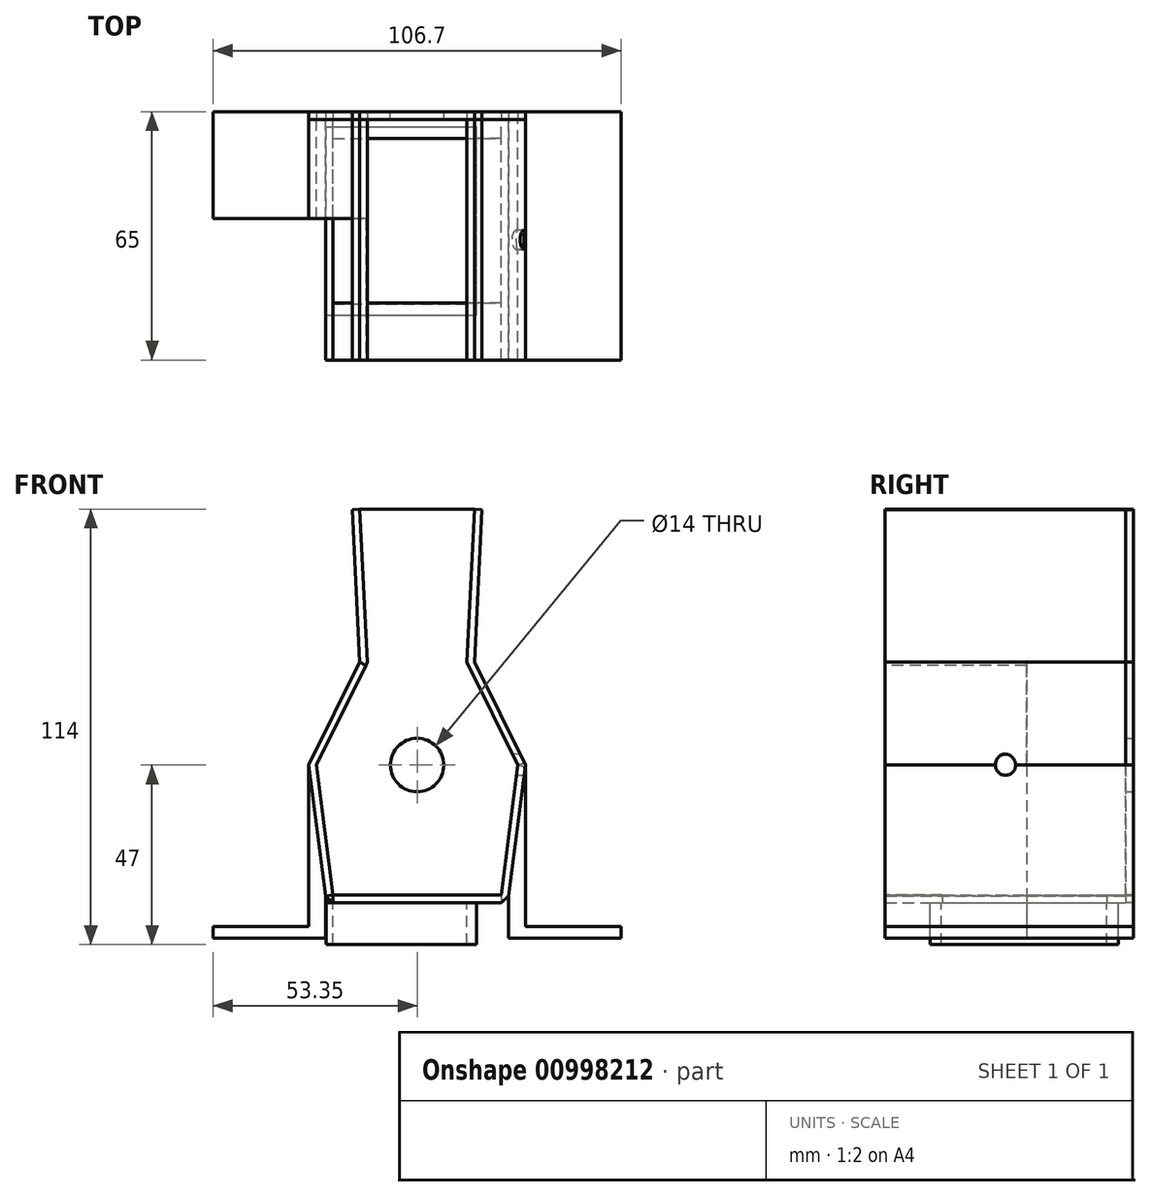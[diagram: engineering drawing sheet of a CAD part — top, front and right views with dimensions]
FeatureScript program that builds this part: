
annotation { "Feature Type Name" : "Feature", "Feature Type Description" : "" }
export const myFeature = defineFeature(function(context is Context, id is Id, definition is map)
    precondition{}
    {
        {
            var Q0;
            Q0=qCreatedBy(makeId("Front.planeOp"),FACE);
            var sketch = newSketch(context, id + "F0", { "sketchPlane" : qUnion([Q0])});
            skLineSegment(sketch, "E0.bottom", {"start": v(0, 0) * mm, "end": v(-26, 0) * mm});
            skLineSegment(sketch, "E0.top", {"start": v(0, 27) * mm, "end": v(-26, 27) * mm});
            skLineSegment(sketch, "E0.left", {"start": v(0, 0) * mm, "end": v(0, 27) * mm});
            skLineSegment(sketch, "E0.right", {"start": v(-26, 0) * mm, "end": v(-26, 27) * mm});
            skLineSegment(sketch, "E1", {"start": v(-26, 0) * mm, "end": v(-39.35, 0) * mm});
            skLineSegment(sketch, "E2", {"start": v(0, 0) * mm, "end": v(13.35, 0) * mm});
            skLineSegment(sketch, "E3", {"start": v(-26, 27) * mm, "end": v(-39.35, 0) * mm});
            skLineSegment(sketch, "E4", {"start": v(0, 27) * mm, "end": v(13.35, 0) * mm});
            skLineSegment(sketch, "E5.bottom", {"start": v(0, 0) * mm, "end": v(-13, 0) * mm});
            skLineSegment(sketch, "E5.top", {"start": v(0, -34) * mm, "end": v(-13, -34) * mm});
            skLineSegment(sketch, "E5.left", {"start": v(0, 0) * mm, "end": v(0, -34) * mm});
            skLineSegment(sketch, "E5.right", {"start": v(-13, 0) * mm, "end": v(-13, -34) * mm});
            skLineSegment(sketch, "E6.bottom", {"start": v(-26, 0) * mm, "end": v(-13, 0) * mm});
            skLineSegment(sketch, "E6.top", {"start": v(-26, -34) * mm, "end": v(-13, -34) * mm});
            skLineSegment(sketch, "E6.left", {"start": v(-26, 0) * mm, "end": v(-26, -34) * mm});
            skLineSegment(sketch, "E7", {"start": v(-26, -34) * mm, "end": v(-35, -34) * mm});
            skLineSegment(sketch, "E8", {"start": v(0, -34) * mm, "end": v(9, -34) * mm});
            skLineSegment(sketch, "E9", {"start": v(-35, -34) * mm, "end": v(-39.35, 0) * mm});
            skLineSegment(sketch, "E10", {"start": v(13.35, 0) * mm, "end": v(9, -34) * mm});
            skCircle(sketch, "E11", {"center": v(-13, 0) * mm, "radius": 7 * mm});
            skLineSegment(sketch, "E12.bottom", {"start": v(-26, 27) * mm, "end": v(0, 27) * mm});
            skLineSegment(sketch, "E12.top", {"start": v(-26, 67) * mm, "end": v(0, 67) * mm});
            skLineSegment(sketch, "E12.left", {"start": v(-26, 27) * mm, "end": v(-26, 67) * mm});
            skLineSegment(sketch, "E12.right", {"start": v(0, 27) * mm, "end": v(0, 67) * mm});
            skLineSegment(sketch, "E13", {"start": v(-26, 67) * mm, "end": v(-28, 67) * mm});
            skLineSegment(sketch, "E14", {"start": v(0, 67) * mm, "end": v(2, 67) * mm});
            skLineSegment(sketch, "E15", {"start": v(-26, 27) * mm, "end": v(-28, 67) * mm});
            skLineSegment(sketch, "E16", {"start": v(2, 67) * mm, "end": v(0, 27) * mm});
            skSolve(sketch);
        }
        {
            var Q0;
            Q0=makeQuery(id+"F0.imprint","IMPRINT",FACE,{"disambiguationData":[TD([[makeQuery(id+"F0.imprint","IMPRINT",EDGE,{"derivedFrom":sQuery(id+"F0.wireOp",EDGE,"E0.top")}),-1.0]])]});
            var Q1;
            Q1=makeQuery(id+"F0.imprint","IMPRINT",FACE,{"disambiguationData":[TD([[makeQuery(id+"F0.imprint","IMPRINT",EDGE,{"derivedFrom":sQuery(id+"F0.wireOp",EDGE,"E12.left")}),1.0]])]});
            var Q2;
            Q2=makeQuery(id+"F0.imprint","IMPRINT",FACE,{"disambiguationData":[TD([[makeQuery(id+"F0.imprint","IMPRINT",EDGE,{"derivedFrom":sQuery(id+"F0.wireOp",EDGE,"E12.right")}),-1.0]])]});
            var Q3;
            Q3=makeQuery(id+"F0.imprint","IMPRINT",FACE,{"disambiguationData":[TD([[makeQuery(id+"F0.imprint","IMPRINT",EDGE,{"derivedFrom":sQuery(id+"F0.wireOp",EDGE,"E0.top")}),1.0]])]});
            var Q4;
            Q4=makeQuery(id+"F0.imprint","IMPRINT",FACE,{"disambiguationData":[TD([[makeQuery(id+"F0.imprint","IMPRINT",EDGE,{"derivedFrom":sQuery(id+"F0.wireOp",EDGE,"E0.right")}),1.0]])]});
            var Q5;
            Q5=makeQuery(id+"F0.imprint","IMPRINT",FACE,{"disambiguationData":[TD([[makeQuery(id+"F0.imprint","IMPRINT",EDGE,{"derivedFrom":sQuery(id+"F0.wireOp",EDGE,"E0.left")}),-1.0]])]});
            var Q6;
            Q6=makeQuery(id+"F0.imprint","IMPRINT",FACE,{"disambiguationData":[TD([[makeQuery(id+"F0.imprint","IMPRINT",EDGE,{"derivedFrom":sQuery(id+"F0.wireOp",EDGE,"E2")}),-1.0]])]});
            var Q7;
            {var subQ1=sQuery(id+"F0.wireOp",EDGE,"E6.top");Q7=makeQuery(id+"F0.imprint","IMPRINT",FACE,{"disambiguationData":[TD([[makeQuery(id+"F0.imprint","IMPRINT",EDGE,{"derivedFrom":subQ1}),1.0]])]});}
            var Q8;
            Q8=makeQuery(id+"F0.imprint","IMPRINT",FACE,{"disambiguationData":[TD([[makeQuery(id+"F0.imprint","IMPRINT",EDGE,{"derivedFrom":sQuery(id+"F0.wireOp",EDGE,"E1")}),1.0]])]});
            var Q9;
            {var subQ1=sQuery(id+"F0.wireOp",EDGE,"E5.top");Q9=makeQuery(id+"F0.imprint","IMPRINT",FACE,{"disambiguationData":[TD([[makeQuery(id+"F0.imprint","IMPRINT",EDGE,{"derivedFrom":subQ1}),-1.0]])]});}
            var Q10;
            Q10 = qSketchRegion(id + "F2", true);
            extrude(context, id + "F1", {"entities" : qUnion([Q0, Q1, Q2, Q3, Q4, Q5, Q6, Q7, Q8, Q9, Q10]), "depth" : 2 * mm, "offsetDistance" : 25 * mm});
        }
        {
            var Q0;
            Q0=makeQuery(id+"F1.opExtrude","CAP_FACE",FACE,{"disambiguationData":[OSD([sQuery(id+"F0.wireOp",EDGE,"E3"),sQuery(id+"F0.wireOp",EDGE,"E4"),sQuery(id+"F0.wireOp",EDGE,"E5.top"),sQuery(id+"F0.wireOp",EDGE,"E6.top"),sQuery(id+"F0.wireOp",EDGE,"E7"),sQuery(id+"F0.wireOp",EDGE,"E8"),sQuery(id+"F0.wireOp",EDGE,"E9"),sQuery(id+"F0.wireOp",EDGE,"E10"),sQuery(id+"F0.wireOp",EDGE,"E11"),sQuery(id+"F0.wireOp",EDGE,"E12.top"),sQuery(id+"F0.wireOp",EDGE,"E13"),sQuery(id+"F0.wireOp",EDGE,"E14"),sQuery(id+"F0.wireOp",EDGE,"E15"),sQuery(id+"F0.wireOp",EDGE,"E16")])],"isStart":false});
            var sketch = newSketch(context, id + "F2", { "sketchPlane" : qUnion([Q0])});
            skLineSegment(sketch, "E17", {"start": v(-28, 67) * mm, "end": v(-30, 66.9) * mm});
            skLineSegment(sketch, "E18", {"start": v(2, 67) * mm, "end": v(4, 66.9) * mm});
            skLineSegment(sketch, "E19", {"start": v(0, 27) * mm, "end": v(2, 26.9) * mm});
            skLineSegment(sketch, "E20", {"start": v(-26, 27) * mm, "end": v(-28, 26.9) * mm});
            skLineSegment(sketch, "E21", {"start": v(-39.35, 0) * mm, "end": v(-41.35, 0) * mm});
            skLineSegment(sketch, "E22", {"start": v(13.35, 0) * mm, "end": v(15.35, 0) * mm});
            skLineSegment(sketch, "E23", {"start": v(-35, -34) * mm, "end": v(-36.98, -34.25) * mm});
            skLineSegment(sketch, "E24", {"start": v(9, -34) * mm, "end": v(10.98, -34.25) * mm});
            skLineSegment(sketch, "E25.bottom", {"start": v(-35, -34) * mm, "end": v(9, -34) * mm});
            skLineSegment(sketch, "E25.top", {"start": v(-35, -36) * mm, "end": v(9, -36) * mm});
            skLineSegment(sketch, "E25.left", {"start": v(-35, -34) * mm, "end": v(-35, -36) * mm});
            skLineSegment(sketch, "E25.right", {"start": v(9, -34) * mm, "end": v(9, -36) * mm});
            skLineSegment(sketch, "E26", {"start": v(-30, 66.9) * mm, "end": v(-28, 26.9) * mm});
            skLineSegment(sketch, "E27", {"start": v(-41.35, 0) * mm, "end": v(-28, 26.9) * mm});
            skLineSegment(sketch, "E28", {"start": v(-41.35, 0) * mm, "end": v(-36.98, -34.25) * mm});
            skLineSegment(sketch, "E29", {"start": v(-36.98, -34.25) * mm, "end": v(-35, -36) * mm});
            skLineSegment(sketch, "E30", {"start": v(15.35, 0) * mm, "end": v(10.98, -34.25) * mm});
            skLineSegment(sketch, "E31", {"start": v(15.35, 0) * mm, "end": v(2, 26.9) * mm});
            skLineSegment(sketch, "E32", {"start": v(4, 66.9) * mm, "end": v(2, 26.9) * mm});
            skLineSegment(sketch, "E33", {"start": v(10.98, -34.25) * mm, "end": v(9, -36) * mm});
            skArc(sketch, "E34", {"start": v(-36.98, -34.25) * mm, "mid": v(-36.32, -35.5) * mm, "end": v(-35, -36) * mm});
            skArc(sketch, "E35", {"start": v(9, -36) * mm, "mid": v(10.32, -35.5) * mm, "end": v(10.98, -34.25) * mm});
            skSolve(sketch);
        }
        {
            var Q0;
            Q0=makeQuery(id+"F2.imprint","IMPRINT",FACE,{"disambiguationData":[TD([[makeQuery(id+"F2.imprint","IMPRINT",EDGE,{"derivedFrom":sQuery(id+"F2.wireOp",EDGE,"E17")}),1.0]])]});
            var Q1;
            Q1=makeQuery(id+"F2.imprint","IMPRINT",FACE,{"disambiguationData":[TD([[makeQuery(id+"F2.imprint","IMPRINT",EDGE,{"derivedFrom":sQuery(id+"F2.wireOp",EDGE,"E20")}),1.0]])]});
            var Q2;
            Q2=makeQuery(id+"F2.imprint","IMPRINT",FACE,{"disambiguationData":[TD([[makeQuery(id+"F2.imprint","IMPRINT",EDGE,{"derivedFrom":sQuery(id+"F2.wireOp",EDGE,"E25.bottom")}),-1.0]])]});
            var Q3;
            Q3=makeQuery(id+"F2.imprint","IMPRINT",FACE,{"disambiguationData":[TD([[makeQuery(id+"F2.imprint","IMPRINT",EDGE,{"derivedFrom":sQuery(id+"F2.wireOp",EDGE,"E21")}),1.0]])]});
            var Q4;
            Q4=makeQuery(id+"F2.imprint","IMPRINT",FACE,{"disambiguationData":[TD([[makeQuery(id+"F2.imprint","IMPRINT",EDGE,{"derivedFrom":sQuery(id+"F2.wireOp",EDGE,"E29")}),-1.0]])]});
            var Q5;
            Q5=makeQuery(id+"F2.imprint","IMPRINT",FACE,{"disambiguationData":[TD([[makeQuery(id+"F2.imprint","IMPRINT",EDGE,{"derivedFrom":sQuery(id+"F2.wireOp",EDGE,"E24")}),-1.0]])]});
            var Q6;
            Q6=makeQuery(id+"F2.imprint","IMPRINT",FACE,{"disambiguationData":[TD([[makeQuery(id+"F2.imprint","IMPRINT",EDGE,{"derivedFrom":sQuery(id+"F2.wireOp",EDGE,"E22")}),-1.0]])]});
            var Q7;
            Q7=makeQuery(id+"F2.imprint","IMPRINT",FACE,{"disambiguationData":[TD([[makeQuery(id+"F2.imprint","IMPRINT",EDGE,{"derivedFrom":sQuery(id+"F2.wireOp",EDGE,"E19")}),-1.0]])]});
            var Q8;
            Q8=makeQuery(id+"F2.imprint","IMPRINT",FACE,{"disambiguationData":[TD([[makeQuery(id+"F2.imprint","IMPRINT",EDGE,{"derivedFrom":sQuery(id+"F2.wireOp",EDGE,"E18")}),-1.0]])]});
            extrude(context, id + "F3", {"entities" : qUnion([Q0, Q1, Q2, Q3, Q4, Q5, Q6, Q7, Q8]), "operationType" : NewBodyOperationType.ADD, "depth" : 63 * mm, "offsetDistance" : 25 * mm});
        }
        {
            var Q0;
            Q0=makeQuery(id+"F3.opExtrude","CAP_FACE",FACE,{"disambiguationData":[OSD([sQuery(id+"F0.wireOp",EDGE,"E4"),sQuery(id+"F0.wireOp",EDGE,"E10"),sQuery(id+"F0.wireOp",EDGE,"E16"),sQuery(id+"F2.wireOp",EDGE,"E18"),sQuery(id+"F2.wireOp",EDGE,"E25.bottom"),sQuery(id+"F2.wireOp",EDGE,"E25.top"),sQuery(id+"F2.wireOp",EDGE,"E25.left"),sQuery(id+"F2.wireOp",EDGE,"E30"),sQuery(id+"F2.wireOp",EDGE,"E31"),sQuery(id+"F2.wireOp",EDGE,"E32"),sQuery(id+"F2.wireOp",EDGE,"E33")])],"isStart":true});
            var Q1;
            Q1=makeQuery(id+"F3.opExtrude","CAP_FACE",FACE,{"disambiguationData":[OSD([sQuery(id+"F0.wireOp",EDGE,"E3"),sQuery(id+"F0.wireOp",EDGE,"E9"),sQuery(id+"F0.wireOp",EDGE,"E15"),sQuery(id+"F2.wireOp",EDGE,"E17"),sQuery(id+"F2.wireOp",EDGE,"E23"),sQuery(id+"F2.wireOp",EDGE,"E26"),sQuery(id+"F2.wireOp",EDGE,"E27"),sQuery(id+"F2.wireOp",EDGE,"E28")])],"isStart":true});
            extrude(context, id + "F4", {"entities" : qUnion([Q0, Q1]), "depth" : 2 * mm, "offsetDistance" : 25 * mm});
        }
        {
            var Q0;
            Q0=makeQuery(id+"F3.opExtrude","SWEPT_FACE",FACE,{"disambiguationData":[OSD([sQuery(id+"F2.wireOp",EDGE,"E27")])]});
            var sketch = newSketch(context, id + "F5", { "sketchPlane" : qUnion([Q0])});
            skLineSegment(sketch, "E36", {"start": v(28, 11.65) * mm, "end": v(28, -18.38) * mm});
            skLineSegment(sketch, "E37", {"start": v(28, 11.65) * mm, "end": v(65, 11.65) * mm});
            skLineSegment(sketch, "E38", {"start": v(65, 11.65) * mm, "end": v(65, -18.38) * mm});
            skLineSegment(sketch, "E39", {"start": v(65, -18.38) * mm, "end": v(28, -18.38) * mm});
            skSolve(sketch);
        }
        {
            var Q0;
            Q0=makeQuery(id+"F5.imprint","IMPRINT",FACE,{"disambiguationData":[TD([[makeQuery(id+"F5.imprint","IMPRINT",EDGE,{"derivedFrom":sQuery(id+"F5.wireOp",EDGE,"E36")}),1.0]])]});
            extrude(context, id + "F6", {"entities" : qUnion([Q0]), "operationType" : NewBodyOperationType.REMOVE, "oppositeDirection" : true, "depth" : 3 * mm, "offsetDistance" : 25 * mm});
        }
        {
            var Q0;
            Q0=makeQuery(id+"F3.opExtrude","SWEPT_FACE",FACE,{"disambiguationData":[OSD([sQuery(id+"F2.wireOp",EDGE,"E28")])]});
            var sketch = newSketch(context, id + "F7", { "sketchPlane" : qUnion([Q0])});
            skLineSegment(sketch, "E40", {"start": v(28, 5.23) * mm, "end": v(28, -29.3) * mm});
            skLineSegment(sketch, "E41", {"start": v(28, -29.3) * mm, "end": v(65, -29.3) * mm});
            skLineSegment(sketch, "E42", {"start": v(65, -29.3) * mm, "end": v(65, 5.23) * mm});
            skSolve(sketch);
        }
        {
            var Q0;
            Q0=makeQuery(id+"F7.imprint","IMPRINT",FACE,{"disambiguationData":[TD([[makeQuery(id+"F7.imprint","IMPRINT",EDGE,{"derivedFrom":sQuery(id+"F7.wireOp",EDGE,"E40")}),1.0]])]});
            extrude(context, id + "F8", {"entities" : qUnion([Q0]), "operationType" : NewBodyOperationType.REMOVE, "oppositeDirection" : true, "depth" : 3 * mm, "offsetDistance" : 25 * mm});
        }
        {
            var Q0;
            Q0=makeQuery(id+"F3.opExtrude","SWEPT_FACE",FACE,{"disambiguationData":[OSD([sQuery(id+"F2.wireOp",EDGE,"E30")])]});
            var sketch = newSketch(context, id + "F9", { "sketchPlane" : qUnion([Q0])});
            skCircle(sketch, "E43", {"center": v(-33.5, 1.94) * mm, "radius": 2.65 * mm});
            skSolve(sketch);
        }
        {
            var Q0;
            {var subQ0=sQuery(id+"F9.wireOp",EDGE,"E43");var subQ1=makeQuery(id+"F3.opExtrude","SWEPT_EDGE",EDGE,{"disambiguationData":[OSD([sQuery(id+"F2.wireOp",EDGE,"E22"),sQuery(id+"F2.wireOp",EDGE,"E30"),sQuery(id+"F2.wireOp",EDGE,"E31")])]});var subQ2=makeQuery(id+"F9.imprint","INTERSECT",VERTEX,{"disambiguationData":[OD(0.0)],"derivedFrom":[subQ1,subQ0]});Q0=makeQuery(id+"F9.imprint","IMPRINT",FACE,{"disambiguationData":[TD([[makeQuery(id+"F9.imprint","IMPRINT",EDGE,{"disambiguationData":[TD([[subQ2,1.0]])],"derivedFrom":subQ0}),1.0]])]});}
            var Q1;
            {var subQ0=sQuery(id+"F9.wireOp",EDGE,"E43");var subQ1=makeQuery(id+"F3.opExtrude","SWEPT_EDGE",EDGE,{"disambiguationData":[OSD([sQuery(id+"F2.wireOp",EDGE,"E22"),sQuery(id+"F2.wireOp",EDGE,"E30"),sQuery(id+"F2.wireOp",EDGE,"E31")])]});var subQ2=makeQuery(id+"F9.imprint","INTERSECT",VERTEX,{"disambiguationData":[OD(0.0)],"derivedFrom":[subQ1,subQ0]});Q1=makeQuery(id+"F9.imprint","IMPRINT",FACE,{"disambiguationData":[TD([[makeQuery(id+"F9.imprint","IMPRINT",EDGE,{"disambiguationData":[TD([[subQ2,-1.0]])],"derivedFrom":subQ0}),1.0]])]});}
            extrude(context, id + "F10", {"entities" : qUnion([Q0, Q1]), "operationType" : NewBodyOperationType.REMOVE, "oppositeDirection" : true, "depth" : 5 * mm, "offsetDistance" : 25 * mm});
        }
        {
            var Q0;
            Q0=makeQuery(id+"F3.opExtrude","CAP_FACE",FACE,{"disambiguationData":[OSD([sQuery(id+"F0.wireOp",EDGE,"E4"),sQuery(id+"F0.wireOp",EDGE,"E10"),sQuery(id+"F0.wireOp",EDGE,"E16"),sQuery(id+"F2.wireOp",EDGE,"E18"),sQuery(id+"F2.wireOp",EDGE,"E25.bottom"),sQuery(id+"F2.wireOp",EDGE,"E25.top"),sQuery(id+"F2.wireOp",EDGE,"E25.left"),sQuery(id+"F2.wireOp",EDGE,"E30"),sQuery(id+"F2.wireOp",EDGE,"E31"),sQuery(id+"F2.wireOp",EDGE,"E32"),sQuery(id+"F2.wireOp",EDGE,"E33")])],"isStart":false});
            var sketch = newSketch(context, id + "F11", { "sketchPlane" : qUnion([Q0])});
            skLineSegment(sketch, "E44", {"start": v(15.35, 0) * mm, "end": v(15.35, -45.25) * mm});
            skLineSegment(sketch, "E45", {"start": v(15.35, -45.25) * mm, "end": v(10.98, -45.25) * mm});
            skLineSegment(sketch, "E46", {"start": v(10.98, -45.25) * mm, "end": v(10.98, -34.25) * mm});
            skSolve(sketch);
        }
        {
            var Q0;
            Q0=makeQuery(id+"F11.imprint","IMPRINT",FACE,{"disambiguationData":[TD([[makeQuery(id+"F11.imprint","IMPRINT",EDGE,{"derivedFrom":sQuery(id+"F11.wireOp",EDGE,"E44")}),-1.0]])]});
            extrude(context, id + "F12", {"entities" : qUnion([Q0]), "oppositeDirection" : true, "depth" : 65 * mm, "offsetDistance" : 25 * mm});
        }
        {
            var Q0;
            Q0=makeQuery(id+"F12.opExtrude","SWEPT_FACE",FACE,{"disambiguationData":[OSD([sQuery(id+"F11.wireOp",EDGE,"E44")])]});
            var sketch = newSketch(context, id + "F13", { "sketchPlane" : qUnion([Q0])});
            skLineSegment(sketch, "E47.bottom", {"start": v(-65, -45.25) * mm, "end": v(0, -45.25) * mm});
            skLineSegment(sketch, "E47.top", {"start": v(-65, -42.25) * mm, "end": v(0, -42.25) * mm});
            skLineSegment(sketch, "E47.left", {"start": v(-65, -45.25) * mm, "end": v(-65, -42.25) * mm});
            skLineSegment(sketch, "E47.right", {"start": v(0, -45.25) * mm, "end": v(0, -42.25) * mm});
            skSolve(sketch);
        }
        {
            var Q0;
            Q0=makeQuery(id+"F13.imprint","IMPRINT",FACE,{"disambiguationData":[TD([[makeQuery(id+"F13.imprint","IMPRINT",EDGE,{"derivedFrom":sQuery(id+"F13.wireOp",EDGE,"E47.bottom")}),-1.0]])]});
            extrude(context, id + "F14", {"entities" : qUnion([Q0]), "operationType" : NewBodyOperationType.ADD, "depth" : 25 * mm, "offsetDistance" : 25 * mm});
        }
        {
            var Q0;
            Q0=makeQuery(id+"F4.opExtrude","CAP_FACE",FACE,{"disambiguationData":[OSD([sQuery(id+"F0.wireOp",EDGE,"E3"),sQuery(id+"F0.wireOp",EDGE,"E9"),sQuery(id+"F0.wireOp",EDGE,"E15"),sQuery(id+"F2.wireOp",EDGE,"E17"),sQuery(id+"F2.wireOp",EDGE,"E23"),sQuery(id+"F2.wireOp",EDGE,"E26"),sQuery(id+"F2.wireOp",EDGE,"E27"),sQuery(id+"F2.wireOp",EDGE,"E28")])],"isStart":false});
            var sketch = newSketch(context, id + "F15", { "sketchPlane" : qUnion([Q0])});
            skLineSegment(sketch, "E48", {"start": v(41.35, 0) * mm, "end": v(41.35, -42.27) * mm});
            skLineSegment(sketch, "E49", {"start": v(36.98, -34.25) * mm, "end": v(36.98, -45.25) * mm});
            skLineSegment(sketch, "E50", {"start": v(41.35, -45.25) * mm, "end": v(36.98, -45.25) * mm});
            skLineSegment(sketch, "E51", {"start": v(41.35, -42.27) * mm, "end": v(66.35, -42.27) * mm});
            skLineSegment(sketch, "E52", {"start": v(66.35, -42.27) * mm, "end": v(66.35, -45.27) * mm});
            skLineSegment(sketch, "E53", {"start": v(66.35, -45.27) * mm, "end": v(41.35, -45.25) * mm});
            skSolve(sketch);
        }
        {
            var Q0;
            Q0=makeQuery(id+"F15.imprint","IMPRINT",FACE,{"disambiguationData":[TD([[makeQuery(id+"F15.imprint","IMPRINT",EDGE,{"derivedFrom":sQuery(id+"F15.wireOp",EDGE,"E48")}),-1.0]])]});
            extrude(context, id + "F16", {"entities" : qUnion([Q0]), "oppositeDirection" : true, "depth" : 28 * mm, "offsetDistance" : 25 * mm});
        }
        {
            var Q0;
            Q0=makeQuery(id+"F12.opExtrude","SWEPT_FACE",FACE,{"disambiguationData":[OSD([sQuery(id+"F11.wireOp",EDGE,"E44")])]});
            var sketch = newSketch(context, id + "F17", { "sketchPlane" : qUnion([Q0])});
            skCircle(sketch, "E54", {"center": v(-33.49, 0) * mm, "radius": 2.65 * mm});
            skSolve(sketch);
        }
        {
            var Q0;
            {var subQ0=sQuery(id+"F17.wireOp",EDGE,"E54");var subQ1=makeQuery(id+"F12.opExtrude","SWEPT_EDGE",EDGE,{"disambiguationData":[OSD([sQuery(id+"F2.wireOp",EDGE,"E30"),sQuery(id+"F2.wireOp",EDGE,"E31"),sQuery(id+"F11.wireOp",EDGE,"E44")])]});var subQ2=makeQuery(id+"F17.imprint","INTERSECT",VERTEX,{"disambiguationData":[OD(0.0)],"derivedFrom":[subQ1,subQ0]});Q0=makeQuery(id+"F17.imprint","IMPRINT",FACE,{"disambiguationData":[TD([[makeQuery(id+"F17.imprint","IMPRINT",EDGE,{"disambiguationData":[TD([[subQ2,-1.0]])],"derivedFrom":subQ0}),1.0]])]});}
            var Q1;
            {var subQ0=sQuery(id+"F17.wireOp",EDGE,"E54");var subQ1=makeQuery(id+"F12.opExtrude","SWEPT_EDGE",EDGE,{"disambiguationData":[OSD([sQuery(id+"F2.wireOp",EDGE,"E30"),sQuery(id+"F2.wireOp",EDGE,"E31"),sQuery(id+"F11.wireOp",EDGE,"E44")])]});var subQ2=makeQuery(id+"F17.imprint","INTERSECT",VERTEX,{"disambiguationData":[OD(0.0)],"derivedFrom":[subQ1,subQ0]});Q1=makeQuery(id+"F17.imprint","IMPRINT",FACE,{"disambiguationData":[TD([[makeQuery(id+"F17.imprint","IMPRINT",EDGE,{"disambiguationData":[TD([[subQ2,1.0]])],"derivedFrom":subQ0}),1.0]])]});}
            extrude(context, id + "F18", {"entities" : qUnion([Q0, Q1]), "operationType" : NewBodyOperationType.REMOVE, "oppositeDirection" : true, "depth" : 5 * mm, "offsetDistance" : 25 * mm});
        }
        {
            var Q0;
            Q0=makeQuery(id+"F3.opExtrude","SWEPT_FACE",FACE,{"disambiguationData":[OSD([sQuery(id+"F2.wireOp",EDGE,"E25.top")])]});
            var sketch = newSketch(context, id + "F19", { "sketchPlane" : qUnion([Q0])});
            skLineSegment(sketch, "E55.bottom", {"start": v(9, 7) * mm, "end": v(-35, 7) * mm});
            skLineSegment(sketch, "E55.top", {"start": v(9, 50) * mm, "end": v(-35, 50) * mm});
            skLineSegment(sketch, "E55.left", {"start": v(9, 7) * mm, "end": v(9, 50) * mm});
            skLineSegment(sketch, "E55.right", {"start": v(-35, 7) * mm, "end": v(-35, 50) * mm});
            skSolve(sketch);
        }
        {
            var Q0;
            Q0=makeQuery(id+"F19.imprint","IMPRINT",FACE,{"disambiguationData":[TD([[makeQuery(id+"F19.imprint","IMPRINT",EDGE,{"derivedFrom":sQuery(id+"F19.wireOp",EDGE,"E55.bottom")}),-1.0]])]});
            extrude(context, id + "F20", {"entities" : qUnion([Q0]), "operationType" : NewBodyOperationType.REMOVE, "oppositeDirection" : true, "depth" : 3 * mm, "offsetDistance" : 25 * mm});
        }
        {
            var Q0;
            {var subQ2=sQuery(id+"F2.wireOp",EDGE,"E25.top");Q0=makeQuery(id+"F20.boolean.opBoolean","SPLIT",FACE,{"disambiguationData":[TD([makeQuery(id+"F20.opExtrude","SWEPT_FACE",FACE,{"disambiguationData":[OSD([sQuery(id+"F19.wireOp",EDGE,"E55.bottom")])]})])],"derivedFrom":makeQuery(id+"F3.opExtrude","SWEPT_FACE",FACE,{"disambiguationData":[OSD([subQ2])]})});}
            var sketch = newSketch(context, id + "F21", { "sketchPlane" : qUnion([Q0])});
            skLineSegment(sketch, "E56.bottom", {"start": v(-35.1, 50.32) * mm, "end": v(0, 50.32) * mm});
            skLineSegment(sketch, "E56.top", {"start": v(-35.1, 7) * mm, "end": v(0, 7) * mm});
            skLineSegment(sketch, "E56.left", {"start": v(-35.1, 50.32) * mm, "end": v(-35.1, 7) * mm});
            skLineSegment(sketch, "E56.right", {"start": v(0, 50.32) * mm, "end": v(0, 7) * mm});
            skLineSegment(sketch, "E57.bottom", {"start": v(-36.84, 53.26) * mm, "end": v(2.53, 53.26) * mm});
            skLineSegment(sketch, "E57.top", {"start": v(-36.84, 4) * mm, "end": v(2.53, 4) * mm});
            skLineSegment(sketch, "E57.left", {"start": v(-36.84, 53.26) * mm, "end": v(-36.84, 4) * mm});
            skLineSegment(sketch, "E57.right", {"start": v(2.53, 53.26) * mm, "end": v(2.53, 4) * mm});
            skSolve(sketch);
        }
        {
            var Q0;
            Q0=makeQuery(id+"F21.imprint","IMPRINT",FACE,{"disambiguationData":[TD([[makeQuery(id+"F21.imprint","IMPRINT",EDGE,{"derivedFrom":sQuery(id+"F21.wireOp",EDGE,"E56.bottom")}),1.0]])]});
            var Q1;
            {var subQ4=sQuery(id+"F21.wireOp",EDGE,"E57.right");var subQ6=sQuery(id+"F21.wireOp",EDGE,"E57.top");var subQ7=makeQuery(id+"F21.imprint","INTERSECT",VERTEX,{"derivedFrom":[subQ6,subQ4]});Q1=makeQuery(id+"F21.imprint","IMPRINT",FACE,{"disambiguationData":[TD([[makeQuery(id+"F21.imprint","IMPRINT",EDGE,{"disambiguationData":[TD([[subQ7,1.0]])],"derivedFrom":subQ4}),-1.0]])]});}
            extrude(context, id + "F22", {"entities" : qUnion([Q0, Q1]), "operationType" : NewBodyOperationType.ADD, "depth" : 11 * mm, "offsetDistance" : 25 * mm});
        }
    });
